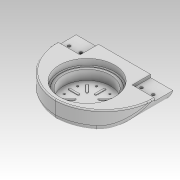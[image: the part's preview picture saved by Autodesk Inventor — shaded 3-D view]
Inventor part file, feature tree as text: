
AUTODESK INVENTOR PART (.ipt)
format: ipt  version: 2020 (Build 240168000, 168)  size: 692,224 bytes
history: native  units: mm
features: sketch x15, extrude x14, fillet x4, projected_geometry x4, revolve x1, mirror x1, plane x1, pattern_circular x1, chamfer x1
ambient origin geometry x8: Origin, YZ Plane, XZ Plane, XY Plane, X Axis, Y Axis, Z Axis, Center Point
bodies: Solid1 (feature_tree)
feature tree (42):
  extrude  "Extrusion1"  Depth=170.0mm
  extrude  "Extrusion2"  Depth=33.0mm
  extrude  "Extrusion3"  Depth=12.0mm
  sketch  "Sketch4"  dims[d8=20.0mm d9=0.0mm d10=0.0mm]
  revolve  "Revolution1"  [1 undecoded]
  extrude  "Extrusion4"  Depth=47.55mm
  extrude  "Extrusion5"  Depth=3.0mm
  fillet  "Fillet1"  Radius=1.0mm
  extrude  "Extrusion8"  Depth=17.5mm
  mirror  "Mirror1"
  extrude  "Extrusion6"  TaperAngle=90.0deg  [1 undecoded]
  extrude  "Extrusion7"  Depth=0.6mm
  extrude  "Extrusion9"  Depth=7.0mm
  fillet  "Fillet3"  Radius=1.5mm
  fillet  "Fillet4"  Radius=1.5mm
  extrude  "Extrusion10"  Depth=2.0mm
  plane  "Work Plane1"
  extrude  "Extrusion11"  Depth=60.0mm
  pattern_circular  "Circular Pattern1"  Count=2  [1 undecoded]
  extrude  "Extrusion12"  Depth=104.0mm
  extrude  "Extrusion13"  TaperAngle=45.0deg  [1 undecoded]
  fillet  "Fillet5"  Radius=6.4mm
  extrude  "Extrusion14"  Depth=10.0mm TaperAngle=0.0deg
  chamfer  "Chamfer2"  Distance=10.0mm
  sketch  "Sketch1"  dims[d0=170.0mm d1=170.0mm]
  sketch  "Sketch2"  dims[d2=40.0mm d3=33.0mm]
  projected_geometry  "Projected Loop1"
  projected_geometry  "Projected Loop2"
  sketch  "Sketch3"  dims[d4=120.0mm d5=0.0mm d7=12.0mm]
  projected_geometry  "Projected Loop3"
  sketch  "Sketch5"  dims[d11=0.0mm d12=0.0mm d13=47.55mm]
  sketch  "Sketch6"  dims[d14=10.1mm d15=3.0mm d16=1.0mm]
  projected_geometry  "Projected Loop4"
  sketch  "Sketch7"  dims[d17=40.2mm d18=17.5mm]
  sketch  "Sketch8"  dims[d19=65.0mm d20=90.0deg]
  sketch  "Sketch9"  dims[d21=11.05mm d22=0.6mm]
  sketch  "Sketch10"  dims[d23=1.5mm d25=7.0mm d26=1.5mm d27=1.5mm]
  sketch  "Sketch11"  dims[d29=35.0mm d30=2.0mm]
  sketch  "Sketch12"  dims[d31=14.9mm d32=60.0mm d33=20.0mm]
  sketch  "Sketch13"  dims[d34=5.0mm d35=0.0mm d36=104.0mm]
  sketch  "Sketch14"  dims[d37=8.0mm d38=45.0deg d39=6.4mm]
  sketch  "Sketch15"  dims[d40=40.0mm d42=360.0deg d44=12.5mm d45=0.0mm d46=10.0mm d47=5.0mm d48=0.0mm d49=137.0mm d50=0.0mm d51=5.0mm d52=12.0mm d53=7.0mm d54=5.0mm d55=17.0mm d56=0.0mm d57=0.0mm d58=15.0mm d59=2.0mm d60=22.5mm d65=0.8mm d66=0.0mm d68=10.0mm d70=30.0mm d71=3.5mm d72=0.0mm d73=0.0mm d74=0.5mm d75=22.5deg d76=-2.0mm d77=6.0mm d78=2.0mm d79=0.0mm d80=80.0mm d81=360.0deg d83=1.0mm d84=1.0mm d85=0.5mm d86=0.0mm d87=15.0mm d88=15.0mm d89=15.0mm d90=3.8mm d91=10.0mm d92=0.0mm d93=2.0mm d97=0.3mm d98=0.2mm d99=0.2mm d100=0.3mm d101=10.0mm d102=0.0mm d103=0.5mm d104=2.0mm d105=45.0deg d106=8.0mm]
note: 4 required parameter values undecoded (feature->parameter linkage not recoverable at this tier; creation-order binding heuristic only, values carry confidence <= 0.55)